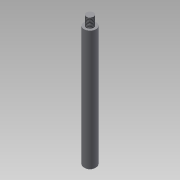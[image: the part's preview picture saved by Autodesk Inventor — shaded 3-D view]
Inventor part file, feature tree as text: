
AUTODESK INVENTOR PART (.ipt)
format: ipt  version: 2014 (Build 180170000, 170)  size: 74,752 bytes
history: native  units: mm
features: extrude x2, sketch x2, thread x1, chamfer x1
ambient origin geometry x8: Origin, YZ Plane, XZ Plane, XY Plane, X Axis, Y Axis, Z Axis, Center Point
bodies: Solid1 (feature_tree)
feature tree (6):
  extrude  "Extrusion1"  Depth=100.0mm TaperAngle=0.0deg
  extrude  "Extrusion2"  Depth=8.0mm TaperAngle=0.0deg
  thread  "Thread1"  [1 undecoded]
  chamfer  "Chamfer1"  Distance=1.0mm Angle=45.0deg
  sketch  "Sketch1"  dims[d0=10.0mm d1=100.0mm d2=0.0mm]
  sketch  "Sketch3"  dims[d3=6.0mm d4=8.0mm d5=0.0mm d6=10.0mm d7=0.0mm d8=1.0mm d9=2.0mm d10=45.0deg]
note: 1 required parameter value undecoded (feature->parameter linkage not recoverable at this tier; creation-order binding heuristic only, values carry confidence <= 0.55)
